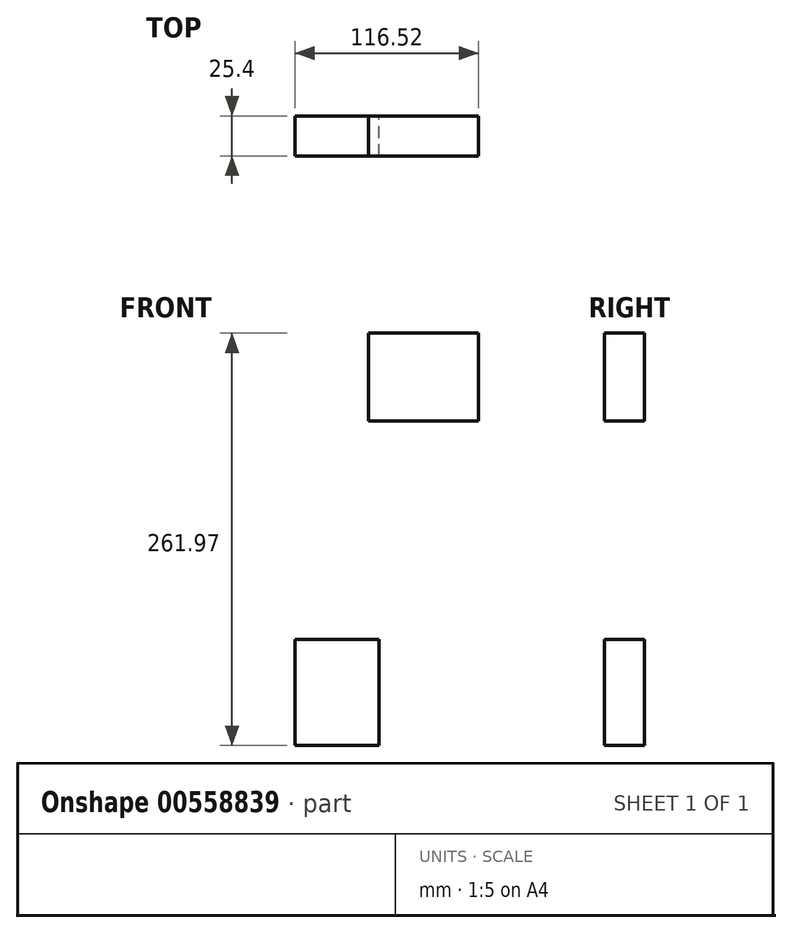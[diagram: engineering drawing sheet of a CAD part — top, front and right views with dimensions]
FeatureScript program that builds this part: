
annotation { "Feature Type Name" : "Feature", "Feature Type Description" : "" }
export const myFeature = defineFeature(function(context is Context, id is Id, definition is map)
    precondition{}
    {
        {
            var Q0;
            Q0=qCreatedBy(makeId("Front.planeOp"),FACE);
            var sketch = newSketch(context, id + "F0", { "sketchPlane" : qUnion([Q0])});
            skLineSegment(sketch, "E0.bottom", {"start": v(-177.78, -56.07) * mm, "end": v(-124.44, -56.07) * mm});
            skLineSegment(sketch, "E0.top", {"start": v(-177.78, -123.38) * mm, "end": v(-124.44, -123.38) * mm});
            skLineSegment(sketch, "E0.left", {"start": v(-177.78, -56.07) * mm, "end": v(-177.78, -123.38) * mm});
            skLineSegment(sketch, "E0.right", {"start": v(-124.44, -56.07) * mm, "end": v(-124.44, -123.38) * mm});
            skLineSegment(sketch, "E1.bottom", {"start": v(-61.26, 82.71) * mm, "end": v(-131.1, 82.71) * mm});
            skLineSegment(sketch, "E1.top", {"start": v(-61.26, 138.6) * mm, "end": v(-131.1, 138.6) * mm});
            skLineSegment(sketch, "E1.left", {"start": v(-61.26, 82.71) * mm, "end": v(-61.26, 138.6) * mm});
            skLineSegment(sketch, "E1.right", {"start": v(-131.1, 82.71) * mm, "end": v(-131.1, 138.6) * mm});
            skSolve(sketch);
        }
        {
            var Q0;
            Q0=makeQuery(id+"F0.imprint","IMPRINT",FACE,{"disambiguationData":[TD([[makeQuery(id+"F0.imprint","IMPRINT",EDGE,{"derivedFrom":sQuery(id+"F0.wireOp",EDGE,"E0.bottom")}),-1.0]])]});
            var Q1;
            Q1=makeQuery(id+"F0.imprint","IMPRINT",FACE,{"disambiguationData":[TD([[makeQuery(id+"F0.imprint","IMPRINT",EDGE,{"derivedFrom":sQuery(id+"F0.wireOp",EDGE,"E1.bottom")}),-1.0]])]});
            extrude(context, id + "F1", {"entities" : qUnion([Q0, Q1]), "endBound" : BoundingType.SYMMETRIC, "depth" : 25.4 * mm, "offsetDistance" : 25.4 * mm});
        }
        {
            var Q0;
            Q0=qCreatedBy(makeId("Front.planeOp"),FACE);
            var sketch = newSketch(context, id + "F2", { "sketchPlane" : qUnion([Q0])});
            skLineSegment(sketch, "E2.bottom", {"start": v(-64.97, 38.28) * mm, "end": v(-0.2, 38.28) * mm});
            skLineSegment(sketch, "E2.top", {"start": v(-64.97, -12.52) * mm, "end": v(-0.2, -12.52) * mm});
            skLineSegment(sketch, "E2.left", {"start": v(-64.97, 38.28) * mm, "end": v(-64.97, -12.52) * mm});
            skLineSegment(sketch, "E2.right", {"start": v(-0.2, 38.28) * mm, "end": v(-0.2, -12.52) * mm});
            skPoint(sketch, "E2.middle", {"position": v(-32.58, 12.88) * mm});
            skLineSegment(sketch, "E3.bottom", {"start": v(34.11, 45.54) * mm, "end": v(-33.2, 45.54) * mm});
            skLineSegment(sketch, "E3.top", {"start": v(34.11, 98.88) * mm, "end": v(-33.2, 98.88) * mm});
            skLineSegment(sketch, "E3.left", {"start": v(34.11, 45.54) * mm, "end": v(34.11, 98.88) * mm});
            skLineSegment(sketch, "E3.right", {"start": v(-33.2, 45.54) * mm, "end": v(-33.2, 98.88) * mm});
            skPoint(sketch, "E3.middle", {"position": v(0.46, 72.2) * mm});
            skSolve(sketch);
        }
    });
